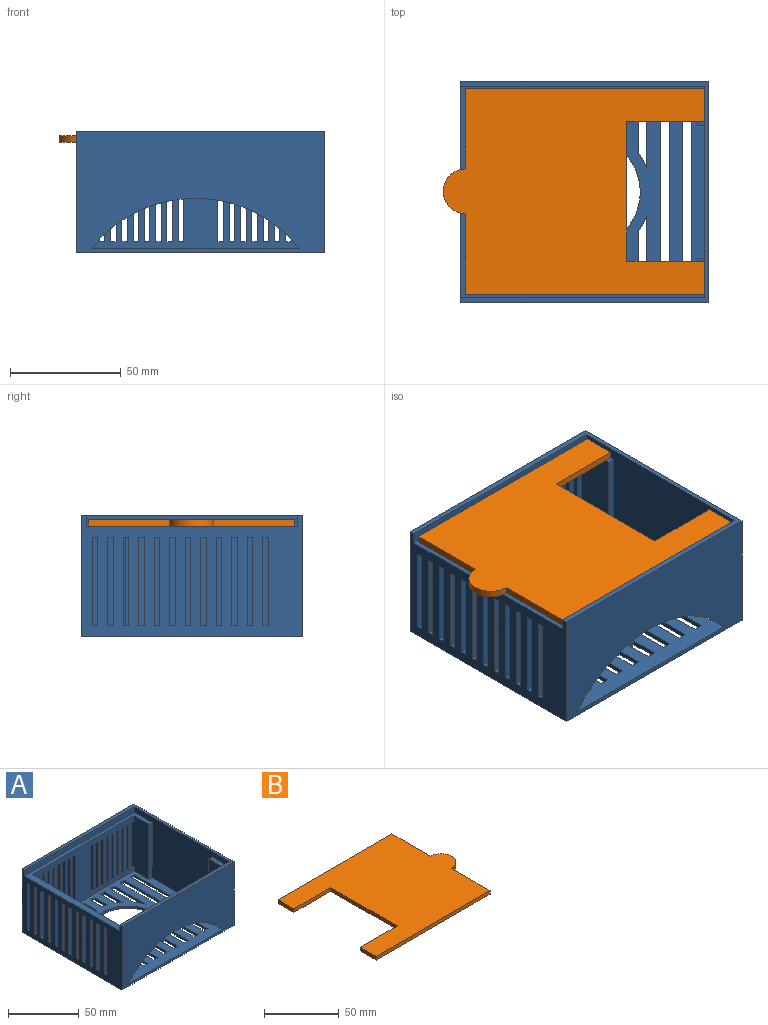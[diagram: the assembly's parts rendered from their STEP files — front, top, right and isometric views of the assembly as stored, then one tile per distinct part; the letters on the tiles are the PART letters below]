
ASSEMBLY  parts=2 mates=1
PART A: 203 faces, bbox 112x100x55 mm
  f0: plane 102x48mm, normal (0,-1,0), area 3096mm2, adj f3,f5,f9,f18,f132,f133,f134,f135
  f1: plane 40x5mm, normal (0,-1,0), area 200mm2, adj f4,f129,f130,f188
  f2: plane 112x55mm, normal (0,1,0), area 4360mm2, adj f4,f6,f7,f9,f11,f132,f133,f134
  f3: plane 90x48mm, normal (1,0,0), area 3120mm2, adj f0,f5,f10,f18,f85,f86,f87,f88
  f4: plane 100x55mm, normal (-1,0,0), area 3825mm2, adj f1,f2,f6,f7,f12,f16,f17,f18
  f5: plane 105x95mm, normal (0,0,1), area 5655mm2, adj f0,f3,f8,f9,f10,f12,f13,f14
  f6: plane 112x100mm, normal (0,0,-1), area 7025.3mm2, adj f2,f4,f11,f12,f19,f20,f21,f22
  f7: plane 112x100mm, normal (0,0,1), area 750mm2, adj f2,f4,f11,f12,f15,f16,f17
  f8: plane 48x15mm, normal (-1,0,0), area 720mm2, adj f5,f10,f14,f18
  f9: plane 48x20mm, normal (-1,0,0), area 920mm2, adj f0,f2,f5,f13,f18,f200,f201
  f10: plane 102x48mm, normal (0,1,0), area 3411.5mm2, adj f3,f5,f8,f18,f84
  f11: plane 100x55mm, normal (1,0,0), area 5500mm2, adj f2,f6,f7,f12
  f12: plane 112x55mm, normal (0,-1,0), area 4675.5mm2, adj f4,f5,f6,f7,f11,f84
  f13: plane 48x3mm, normal (0,-1,0), area 144mm2, adj f5,f9,f15,f18
  f14: plane 48x3mm, normal (0,1,0), area 144mm2, adj f5,f8,f15,f18
  f15: plane 95x53mm, normal (-1,0,0), area 3355mm2, adj f5,f7,f13,f14,f16,f17,f18
  f16: plane 110x5mm, normal (0,-1,0), area 550mm2, adj f4,f7,f15,f18
  f17: plane 110x5mm, normal (0,1,0), area 550mm2, adj f4,f7,f15,f18
  f18: plane 110x95mm, normal (0,0,1), area 1090mm2, adj f0,f3,f4,f8,f9,f10,f13,f14
  f19: plane 21.6x2mm, normal (-1,0,0), area 43.2mm2, adj f5,f6,f20,f22
  f20: cylinder r=30mm len=5.43mm, axis (0,0,1), area 13.5mm2, adj f5,f6,f19,f21
  f21: plane 27.03x2mm, normal (1,0,0), area 54.1mm2, adj f5,f6,f20,f22
  f22: plane 4x2mm, normal (0,1,0), area 8mm2, adj f5,f6,f19,f21
  f23: plane 14.5x2mm, normal (-1,0,0), area 29mm2, adj f5,f6,f24,f26
  f24: cylinder r=30mm len=4mm, axis (0,0,1), area 9.1mm2, adj f5,f6,f23,f25
  f25: plane 16.62x2mm, normal (1,0,0), area 33.2mm2, adj f5,f6,f24,f26
  f26: plane 4x2mm, normal (0,1,0), area 8mm2, adj f5,f6,f23,f25
  f27: plane 4x2mm, normal (0,-1,0), area 8mm2, adj f5,f6,f28,f30
  f28: plane 16.62x2mm, normal (1,0,0), area 33.2mm2, adj f5,f6,f27,f29
  f29: cylinder r=30mm len=4mm, axis (0,0,1), area 9.1mm2, adj f5,f6,f28,f30
  f30: plane 14.5x2mm, normal (-1,0,0), area 29mm2, adj f5,f6,f27,f29
  f31: plane 12.07x2mm, normal (-1,0,0), area 24.1mm2, adj f5,f6,f32,f34
  f32: cylinder r=30mm len=4mm, axis (0,0,1), area 8.1mm2, adj f5,f6,f31,f33
  f33: plane 12.61x2mm, normal (1,0,0), area 25.2mm2, adj f5,f6,f32,f34
  f34: plane 4x2mm, normal (0,1,0), area 8mm2, adj f5,f6,f31,f33
  f35: plane 4x2mm, normal (0,-1,0), area 8mm2, adj f5,f6,f36,f38
  f36: plane 84x2mm, normal (1,0,0), area 168mm2, adj f5,f6,f35,f37
  f37: plane 4x2mm, normal (0,1,0), area 8mm2, adj f5,f6,f36,f38
  f38: plane 84x2mm, normal (-1,0,0), area 168mm2, adj f5,f6,f35,f37
  f39: plane 4x2mm, normal (0,-1,0), area 8mm2, adj f5,f6,f40,f42
  f40: plane 84x2mm, normal (1,0,0), area 168mm2, adj f5,f6,f39,f41
  f41: plane 4x2mm, normal (0,1,0), area 8mm2, adj f5,f6,f40,f42
  f42: plane 84x2mm, normal (-1,0,0), area 168mm2, adj f5,f6,f39,f41
  f43: plane 4x2mm, normal (0,-1,0), area 8mm2, adj f5,f6,f44,f46
  f44: plane 84x2mm, normal (1,0,0), area 168mm2, adj f5,f6,f43,f45
  f45: plane 4x2mm, normal (0,1,0), area 8mm2, adj f5,f6,f44,f46
  f46: plane 84x2mm, normal (-1,0,0), area 168mm2, adj f5,f6,f43,f45
  f47: plane 21.6x2mm, normal (-1,0,0), area 43.2mm2, adj f5,f6,f48,f50
  f48: plane 4x2mm, normal (0,-1,0), area 8mm2, adj f5,f6,f47,f49
  f49: plane 27.03x2mm, normal (1,0,0), area 54.1mm2, adj f5,f6,f48,f50
  f50: cylinder r=30mm len=5.43mm, axis (0,0,1), area 13.5mm2, adj f5,f6,f47,f49
  f51: cylinder r=30mm len=4mm, axis (0,0,1), area 9.5mm2, adj f5,f6,f52,f54
  f52: plane 15.47x2mm, normal (1,0,0), area 30.9mm2, adj f5,f6,f51,f53
  f53: plane 4x2mm, normal (0,1,0), area 8mm2, adj f5,f6,f52,f54
  f54: plane 18x2mm, normal (-1,0,0), area 36mm2, adj f5,f6,f51,f53
  f55: cylinder r=30mm len=7.23mm, axis (0,0,1), area 16.6mm2, adj f5,f6,f56,f58
  f56: plane 24x2mm, normal (1,0,0), area 48mm2, adj f5,f6,f55,f57
  f57: plane 4x2mm, normal (0,1,0), area 8mm2, adj f5,f6,f56,f58
  f58: plane 31.23x2mm, normal (-1,0,0), area 62.5mm2, adj f5,f6,f55,f57
  f59: cylinder r=25mm len=50mm, axis (0,0,1), area 314.2mm2, adj f5,f6
  f60: plane 4x2mm, normal (0,-1,0), area 8mm2, adj f5,f6,f61,f63
  f61: plane 24x2mm, normal (1,0,0), area 48mm2, adj f5,f6,f60,f62
  f62: cylinder r=30mm len=7.23mm, axis (0,0,1), area 16.6mm2, adj f5,f6,f61,f63
  f63: plane 31.23x2mm, normal (-1,0,0), area 62.5mm2, adj f5,f6,f60,f62
  f64: plane 4x2mm, normal (0,-1,0), area 8mm2, adj f5,f6,f65,f67
  f65: plane 12.61x2mm, normal (1,0,0), area 25.2mm2, adj f5,f6,f64,f66
  f66: cylinder r=30mm len=4mm, axis (0,0,1), area 8.1mm2, adj f5,f6,f65,f67
  f67: plane 12.07x2mm, normal (-1,0,0), area 24.1mm2, adj f5,f6,f64,f66
  f68: plane 13.09x2mm, normal (-1,0,0), area 26.2mm2, adj f5,f6,f69,f71
  f69: cylinder r=30mm len=4mm, axis (0,0,1), area 8.2mm2, adj f5,f6,f68,f70
  f70: plane 12.27x2mm, normal (1,0,0), area 24.5mm2, adj f5,f6,f69,f71
  f71: plane 4x2mm, normal (0,1,0), area 8mm2, adj f5,f6,f68,f70
  f72: plane 4x2mm, normal (0,-1,0), area 8mm2, adj f5,f6,f73,f75
  f73: plane 12.27x2mm, normal (1,0,0), area 24.5mm2, adj f5,f6,f72,f74
  f74: cylinder r=30mm len=4mm, axis (0,0,1), area 8.2mm2, adj f5,f6,f73,f75
  f75: plane 13.09x2mm, normal (-1,0,0), area 26.2mm2, adj f5,f6,f72,f74
  f76: plane 4x2mm, normal (0,-1,0), area 8mm2, adj f5,f6,f77,f79
  f77: plane 15.47x2mm, normal (1,0,0), area 30.9mm2, adj f5,f6,f76,f78
  f78: cylinder r=30mm len=4mm, axis (0,0,1), area 9.5mm2, adj f5,f6,f77,f79
  f79: plane 18x2mm, normal (-1,0,0), area 36mm2, adj f5,f6,f76,f78
  f80: plane 4x2mm, normal (0,-1,0), area 8mm2, adj f5,f6,f81,f83
  f81: plane 84x2mm, normal (1,0,0), area 168mm2, adj f5,f6,f80,f82
  f82: plane 4x2mm, normal (0,1,0), area 8mm2, adj f5,f6,f81,f83
  f83: plane 84x2mm, normal (-1,0,0), area 168mm2, adj f5,f6,f80,f82
  f84: cylinder r=60mm len=93.96mm, axis (0,-1,0), area 539.7mm2, adj f5,f10,f12
  f85: plane 40x5mm, normal (0,-1,0), area 200mm2, adj f3,f4,f86,f88
  f86: plane 5x2.5mm, normal (0,0,1), area 12.5mm2, adj f3,f4,f85,f87
  f87: plane 40x5mm, normal (0,1,0), area 200mm2, adj f3,f4,f86,f88
  f88: plane 5x2.5mm, normal (0,0,-1), area 12.5mm2, adj f3,f4,f85,f87
  f89: plane 40x5mm, normal (0,-1,0), area 200mm2, adj f3,f4,f90,f92
  f90: plane 5x2.5mm, normal (0,0,1), area 12.5mm2, adj f3,f4,f89,f91
  f91: plane 40x5mm, normal (0,1,0), area 200mm2, adj f3,f4,f90,f92
  f92: plane 5x2.5mm, normal (0,0,-1), area 12.5mm2, adj f3,f4,f89,f91
  f93: plane 40x5mm, normal (0,-1,0), area 200mm2, adj f3,f4,f94,f96
  f94: plane 5x2.5mm, normal (0,0,1), area 12.5mm2, adj f3,f4,f93,f95
  f95: plane 40x5mm, normal (0,1,0), area 200mm2, adj f3,f4,f94,f96
  f96: plane 5x2.5mm, normal (0,0,-1), area 12.5mm2, adj f3,f4,f93,f95
  f97: plane 40x5mm, normal (0,-1,0), area 200mm2, adj f3,f4,f98,f100
  f98: plane 5x2.5mm, normal (0,0,1), area 12.5mm2, adj f3,f4,f97,f99
  f99: plane 40x5mm, normal (0,1,0), area 200mm2, adj f3,f4,f98,f100
  f100: plane 5x2.5mm, normal (0,0,-1), area 12.5mm2, adj f3,f4,f97,f99
  f101: plane 40x5mm, normal (0,-1,0), area 200mm2, adj f3,f4,f102,f104
  f102: plane 5x2.5mm, normal (0,0,1), area 12.5mm2, adj f3,f4,f101,f103
  f103: plane 40x5mm, normal (0,1,0), area 200mm2, adj f3,f4,f102,f104
  f104: plane 5x2.5mm, normal (0,0,-1), area 12.5mm2, adj f3,f4,f101,f103
  f105: plane 40x5mm, normal (0,-1,0), area 200mm2, adj f3,f4,f106,f108
  f106: plane 5x2.5mm, normal (0,0,1), area 12.5mm2, adj f3,f4,f105,f107
  f107: plane 40x5mm, normal (0,1,0), area 200mm2, adj f3,f4,f106,f108
  f108: plane 5x2.5mm, normal (0,0,-1), area 12.5mm2, adj f3,f4,f105,f107
  f109: plane 40x5mm, normal (0,-1,0), area 200mm2, adj f3,f4,f110,f112
  f110: plane 5x2.5mm, normal (0,0,1), area 12.5mm2, adj f3,f4,f109,f111
  f111: plane 40x5mm, normal (0,1,0), area 200mm2, adj f3,f4,f110,f112
  f112: plane 5x2.5mm, normal (0,0,-1), area 12.5mm2, adj f3,f4,f109,f111
  f113: plane 40x5mm, normal (0,-1,0), area 200mm2, adj f3,f4,f114,f116
  f114: plane 5x2.5mm, normal (0,0,1), area 12.5mm2, adj f3,f4,f113,f115
  f115: plane 40x5mm, normal (0,1,0), area 200mm2, adj f3,f4,f114,f116
  f116: plane 5x2.5mm, normal (0,0,-1), area 12.5mm2, adj f3,f4,f113,f115
  f117: plane 40x5mm, normal (0,-1,0), area 200mm2, adj f3,f4,f118,f120
  f118: plane 5x2.5mm, normal (0,0,1), area 12.5mm2, adj f3,f4,f117,f119
  f119: plane 40x5mm, normal (0,1,0), area 200mm2, adj f3,f4,f118,f120
  f120: plane 5x2.5mm, normal (0,0,-1), area 12.5mm2, adj f3,f4,f117,f119
  f121: plane 40x5mm, normal (0,-1,0), area 200mm2, adj f3,f4,f122,f124
  f122: plane 5x2.5mm, normal (0,0,1), area 12.5mm2, adj f3,f4,f121,f123
  f123: plane 40x5mm, normal (0,1,0), area 200mm2, adj f3,f4,f122,f124
  f124: plane 5x2.5mm, normal (0,0,-1), area 12.5mm2, adj f3,f4,f121,f123
  f125: plane 40x5mm, normal (0,-1,0), area 200mm2, adj f3,f4,f126,f128
  f126: plane 5x2.5mm, normal (0,0,1), area 12.5mm2, adj f3,f4,f125,f127
  f127: plane 40x5mm, normal (0,1,0), area 200mm2, adj f3,f4,f126,f128
  f128: plane 5x2.5mm, normal (0,0,-1), area 12.5mm2, adj f3,f4,f125,f127
  f129: plane 5x2.5mm, normal (0,0,-1), area 12.5mm2, adj f1,f3,f4,f131
  f130: plane 5x2.5mm, normal (0,0,1), area 12.5mm2, adj f1,f3,f4,f131
  f131: plane 40x5mm, normal (0,1,0), area 200mm2, adj f3,f4,f129,f130
  f132: plane 40x5mm, normal (-1,0,0), area 200mm2, adj f0,f2,f133,f135
  f133: plane 5x2.5mm, normal (0,0,1), area 12.5mm2, adj f0,f2,f132,f134
  f134: plane 40x5mm, normal (1,0,0), area 200mm2, adj f0,f2,f133,f135
  f135: plane 5x2.5mm, normal (0,0,-1), area 12.5mm2, adj f0,f2,f132,f134
  f136: plane 40x5mm, normal (-1,0,0), area 200mm2, adj f0,f2,f137,f139
  f137: plane 5x2.5mm, normal (0,0,1), area 12.5mm2, adj f0,f2,f136,f138
  f138: plane 40x5mm, normal (1,0,0), area 200mm2, adj f0,f2,f137,f139
  f139: plane 5x2.5mm, normal (0,0,-1), area 12.5mm2, adj f0,f2,f136,f138
  f140: plane 40x5mm, normal (-1,0,0), area 200mm2, adj f0,f2,f141,f143
  f141: plane 5x2.5mm, normal (0,0,1), area 12.5mm2, adj f0,f2,f140,f142
  f142: plane 40x5mm, normal (1,0,0), area 200mm2, adj f0,f2,f141,f143
  f143: plane 5x2.5mm, normal (0,0,-1), area 12.5mm2, adj f0,f2,f140,f142
  f144: plane 40x5mm, normal (-1,0,0), area 200mm2, adj f0,f2,f145,f147
  f145: plane 5x2.5mm, normal (0,0,1), area 12.5mm2, adj f0,f2,f144,f146
  f146: plane 40x5mm, normal (1,0,0), area 200mm2, adj f0,f2,f145,f147
  f147: plane 5x2.5mm, normal (0,0,-1), area 12.5mm2, adj f0,f2,f144,f146
  f148: plane 40x5mm, normal (-1,0,0), area 200mm2, adj f0,f2,f149,f151
  f149: plane 5x2.5mm, normal (0,0,1), area 12.5mm2, adj f0,f2,f148,f150
  f150: plane 40x5mm, normal (1,0,0), area 200mm2, adj f0,f2,f149,f151
  f151: plane 5x2.5mm, normal (0,0,-1), area 12.5mm2, adj f0,f2,f148,f150
  f152: plane 40x5mm, normal (-1,0,0), area 200mm2, adj f0,f2,f153,f155
  f153: plane 5x2.5mm, normal (0,0,1), area 12.5mm2, adj f0,f2,f152,f154
  f154: plane 40x5mm, normal (1,0,0), area 200mm2, adj f0,f2,f153,f155
  f155: plane 5x2.5mm, normal (0,0,-1), area 12.5mm2, adj f0,f2,f152,f154
  f156: plane 40x5mm, normal (-1,0,0), area 200mm2, adj f0,f2,f157,f159
  f157: plane 5x2.5mm, normal (0,0,1), area 12.5mm2, adj f0,f2,f156,f158
  f158: plane 40x5mm, normal (1,0,0), area 200mm2, adj f0,f2,f157,f159
  f159: plane 5x2.5mm, normal (0,0,-1), area 12.5mm2, adj f0,f2,f156,f158
  f160: plane 40x5mm, normal (-1,0,0), area 200mm2, adj f0,f2,f161,f163
  f161: plane 5x2.5mm, normal (0,0,1), area 12.5mm2, adj f0,f2,f160,f162
  f162: plane 40x5mm, normal (1,0,0), area 200mm2, adj f0,f2,f161,f163
  f163: plane 5x2.5mm, normal (0,0,-1), area 12.5mm2, adj f0,f2,f160,f162
  f164: plane 40x5mm, normal (1,0,0), area 200mm2, adj f0,f2,f165,f167
  f165: plane 5x2.5mm, normal (0,0,-1), area 12.5mm2, adj f0,f2,f164,f166
  f166: plane 40x5mm, normal (-1,0,0), area 200mm2, adj f0,f2,f165,f167
  f167: plane 5x2.5mm, normal (0,0,1), area 12.5mm2, adj f0,f2,f164,f166
  f168: plane 5x2.5mm, normal (0,0,-1), area 12.5mm2, adj f0,f2,f169,f171
  f169: plane 40x5mm, normal (-1,0,0), area 200mm2, adj f0,f2,f168,f170
  f170: plane 5x2.5mm, normal (0,0,1), area 12.5mm2, adj f0,f2,f169,f171
  f171: plane 40x5mm, normal (1,0,0), area 200mm2, adj f0,f2,f168,f170
  f172: plane 40x5mm, normal (1,0,0), area 200mm2, adj f0,f2,f173,f175
  f173: plane 5x2.5mm, normal (0,0,-1), area 12.5mm2, adj f0,f2,f172,f174
  f174: plane 40x5mm, normal (-1,0,0), area 200mm2, adj f0,f2,f173,f175
  f175: plane 5x2.5mm, normal (0,0,1), area 12.5mm2, adj f0,f2,f172,f174
  f176: plane 5x2.5mm, normal (0,0,-1), area 12.5mm2, adj f0,f2,f177,f179
  f177: plane 40x5mm, normal (-1,0,0), area 200mm2, adj f0,f2,f176,f178
  f178: plane 5x2.5mm, normal (0,0,1), area 12.5mm2, adj f0,f2,f177,f179
  f179: plane 40x5mm, normal (1,0,0), area 200mm2, adj f0,f2,f176,f178
  f180: plane 5x2.5mm, normal (0,0,-1), area 12.5mm2, adj f0,f2,f181,f183
  f181: plane 40x5mm, normal (-1,0,0), area 200mm2, adj f0,f2,f180,f182
  f182: plane 5x2.5mm, normal (0,0,1), area 12.5mm2, adj f0,f2,f181,f183
  f183: plane 40x5mm, normal (1,0,0), area 200mm2, adj f0,f2,f180,f182
  f184: plane 5x2.5mm, normal (0,0,-1), area 12.5mm2, adj f0,f2,f185,f187
  f185: plane 40x5mm, normal (-1,0,0), area 200mm2, adj f0,f2,f184,f186
  f186: plane 5x2.5mm, normal (0,0,1), area 12.5mm2, adj f0,f2,f185,f187
  f187: plane 40x5mm, normal (1,0,0), area 200mm2, adj f0,f2,f184,f186
  f188: plane 40x5mm, normal (1,0,0), area 200mm2, adj f1,f2,f189,f191
  f189: plane 5x2.5mm, normal (0,0,-1), area 12.5mm2, adj f0,f2,f188,f190
  f190: plane 40x5mm, normal (-1,0,0), area 200mm2, adj f0,f2,f189,f191
  f191: plane 5x2.5mm, normal (0,0,1), area 12.5mm2, adj f0,f2,f188,f190
  f192: plane 40x5mm, normal (1,0,0), area 200mm2, adj f0,f2,f193,f195
  f193: plane 5x2.5mm, normal (0,0,-1), area 12.5mm2, adj f0,f2,f192,f194
  f194: plane 40x5mm, normal (-1,0,0), area 200mm2, adj f0,f2,f193,f195
  f195: plane 5x2.5mm, normal (0,0,1), area 12.5mm2, adj f0,f2,f192,f194
  f196: plane 5x2.5mm, normal (0,0,-1), area 12.5mm2, adj f0,f2,f197,f199
  f197: plane 40x5mm, normal (-1,0,0), area 200mm2, adj f0,f2,f196,f198
  f198: plane 5x2.5mm, normal (0,0,1), area 12.5mm2, adj f0,f2,f197,f199
  f199: plane 40x5mm, normal (1,0,0), area 200mm2, adj f0,f2,f196,f198
  f200: plane 5x2.5mm, normal (0,0,-1), area 12.5mm2, adj f0,f2,f9,f202
  f201: plane 5x2.5mm, normal (0,0,1), area 12.5mm2, adj f0,f2,f9,f202
  f202: plane 40x5mm, normal (1,0,0), area 200mm2, adj f0,f2,f200,f201
PART B: 12 faces, bbox 118x93x3 mm
  f0: plane 35x3mm, normal (0,1,0), area 105mm2, adj f1,f9,f10,f11
  f1: plane 15x3mm, normal (-1,0,0), area 45mm2, adj f0,f2,f10,f11
  f2: plane 108x3mm, normal (0,-1,0), area 324mm2, adj f1,f3,f10,f11
  f3: plane 36.5x3mm, normal (1,0,0), area 109.5mm2, adj f2,f4,f10,f11
  f4: cylinder r=10mm len=20mm, axis (0,0,-1), area 94.2mm2, adj f3,f5,f10,f11
  f5: plane 36.5x3mm, normal (1,0,0), area 109.5mm2, adj f4,f6,f10,f11
  f6: plane 108x3mm, normal (0,1,0), area 324mm2, adj f5,f7,f10,f11
  f7: plane 15x3mm, normal (-1,0,0), area 45mm2, adj f6,f8,f10,f11
  f8: plane 35x3mm, normal (0,-1,0), area 105mm2, adj f7,f9,f10,f11
  f9: plane 63x3mm, normal (-1,0,0), area 189mm2, adj f0,f8,f10,f11
  f10: plane 118x93mm, normal (0,0,1), area 7996.1mm2, adj f0,f1,f2,f3,f4,f5,f6,f7
  f11: plane 118x93mm, normal (0,0,-1), area 7996.1mm2, adj f0,f1,f2,f3,f4,f5,f6,f7
PLACE A t=(-8.12,-8.62,-33.4)mm
PLACE B rot(axis=(0,0,-1),180deg) t=(-8.12,-8.37,16.6)mm
MATE fastened B.f7 <-> A.f15  axis (1,0,0) through (45.88,-47.37,16.6)mm
